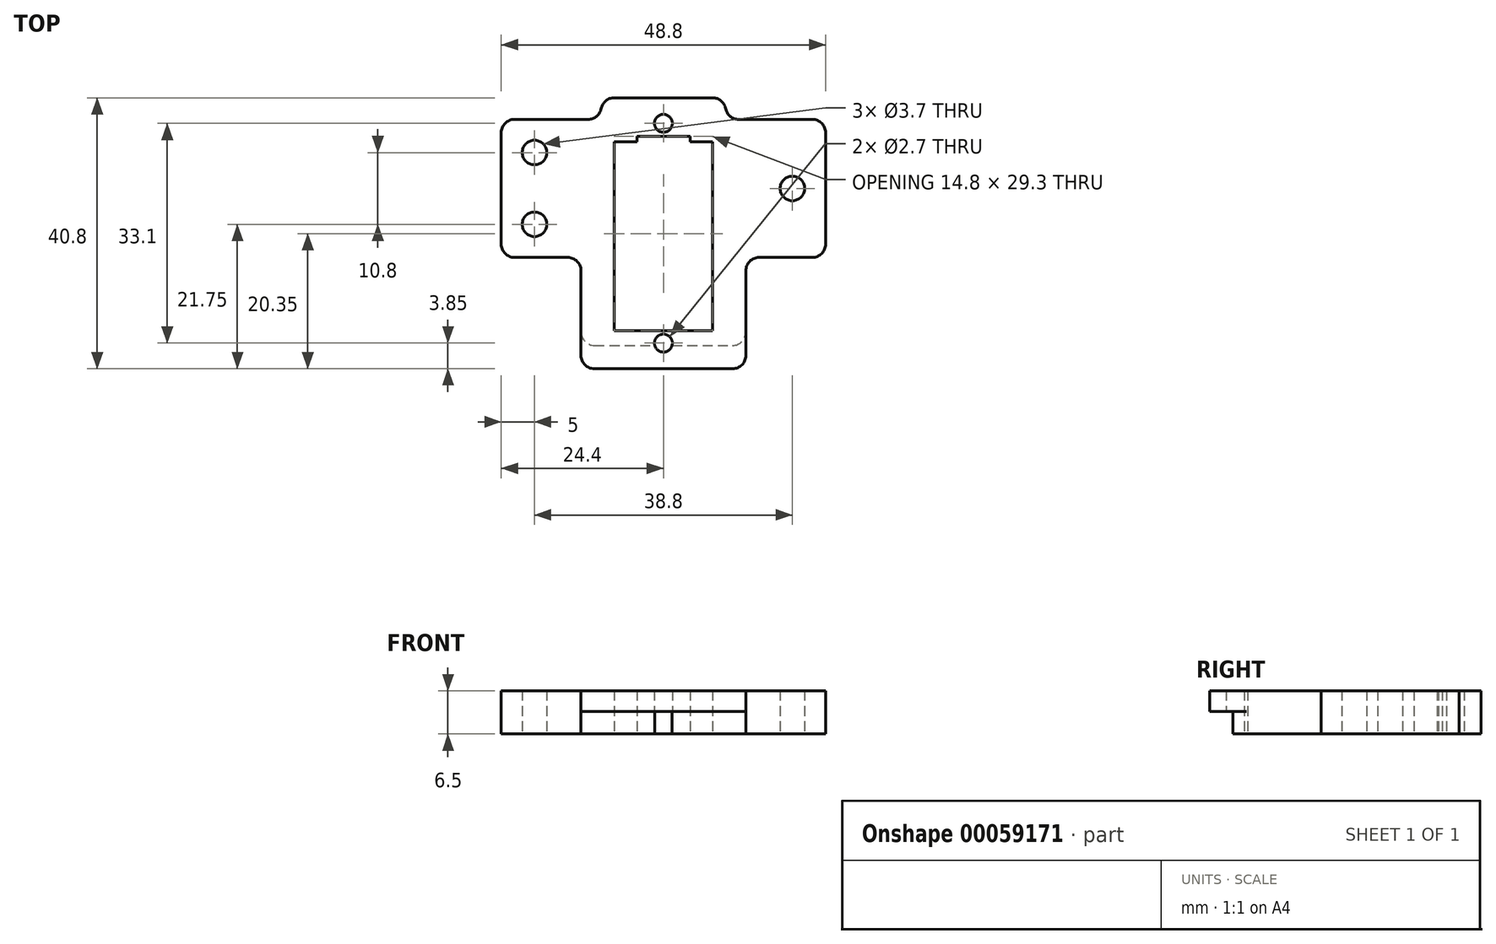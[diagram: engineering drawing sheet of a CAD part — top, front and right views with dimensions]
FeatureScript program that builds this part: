
annotation { "Feature Type Name" : "Feature", "Feature Type Description" : "" }
export const myFeature = defineFeature(function(context is Context, id is Id, definition is map)
    precondition{}
    {
        {
            var Q0;
            Q0=qCreatedBy(makeId("Top.planeOp"),FACE);
            var sketch = newSketch(context, id + "F0", { "sketchPlane" : qUnion([Q0])});
            skLineSegment(sketch, "E0.top", {"start": v(-24.4, -10.4) * mm, "end": v(24.4, -10.4) * mm});
            skLineSegment(sketch, "E0.left", {"start": v(-24.4, 10.4) * mm, "end": v(-24.4, -10.4) * mm});
            skLineSegment(sketch, "E0.right", {"start": v(24.4, 10.4) * mm, "end": v(24.4, -10.4) * mm});
            skCircle(sketch, "E1", {"center": v(-19.4, 5.4) * mm, "radius": 1.85 * mm});
            skCircle(sketch, "E2", {"center": v(-19.4, -5.4) * mm, "radius": 1.85 * mm});
            skLineSegment(sketch, "E3", {"start": v(-9.4, 10.4) * mm, "end": v(-9.4, 13.65) * mm});
            skLineSegment(sketch, "E4", {"start": v(-9.4, 13.65) * mm, "end": v(9.4, 13.65) * mm});
            skLineSegment(sketch, "E5", {"start": v(9.4, 13.65) * mm, "end": v(9.4, 10.4) * mm});
            skLineSegment(sketch, "E6", {"start": v(-9.4, 10.4) * mm, "end": v(-24.4, 10.4) * mm});
            skLineSegment(sketch, "E7", {"start": v(9.4, 10.4) * mm, "end": v(24.4, 10.4) * mm});
            skLineSegment(sketch, "E8", {"start": v(-24.4, -10.4) * mm, "end": v(-24.4, -27.15) * mm});
            skLineSegment(sketch, "E9", {"start": v(-24.4, -27.15) * mm, "end": v(24.5, -27.15) * mm});
            skLineSegment(sketch, "E10", {"start": v(24.5, -27.15) * mm, "end": v(24.4, -10.4) * mm});
            skLineSegment(sketch, "E11.bottom", {"start": v(-7.4, 7.05) * mm, "end": v(7.4, 7.05) * mm});
            skLineSegment(sketch, "E11.top", {"start": v(-7.4, -20.25) * mm, "end": v(7.4, -20.25) * mm});
            skLineSegment(sketch, "E11.left", {"start": v(-7.4, 7.05) * mm, "end": v(-7.4, -20.25) * mm});
            skLineSegment(sketch, "E11.right", {"start": v(7.4, 7.05) * mm, "end": v(7.4, -20.25) * mm});
            skCircle(sketch, "E12", {"center": v(0, 9.8) * mm, "radius": 1.35 * mm});
            skCircle(sketch, "E13", {"center": v(0, -23.3) * mm, "radius": 1.35 * mm});
            skLineSegment(sketch, "E14", {"start": v(-4, 7.05) * mm, "end": v(-4, 7.85) * mm});
            skLineSegment(sketch, "E15", {"start": v(-4, 7.85) * mm, "end": v(4, 7.85) * mm});
            skLineSegment(sketch, "E16", {"start": v(4, 7.85) * mm, "end": v(4, 7.05) * mm});
            skLineSegment(sketch, "E17", {"start": v(-24.4, -23.65) * mm, "end": v(24.48, -23.65) * mm});
            skCircle(sketch, "E18", {"center": v(-27.8, -13.35) * mm, "radius": 2.7 * mm});
            skLineSegment(sketch, "E19", {"start": v(-24.4, -10.4) * mm, "end": v(-33.3, -10.4) * mm});
            skLineSegment(sketch, "E20", {"start": v(-33.3, -10.4) * mm, "end": v(-33.3, -18.51) * mm});
            skLineSegment(sketch, "E21", {"start": v(-33.3, -18.51) * mm, "end": v(-24.4, -23.65) * mm});
            skLineSegment(sketch, "E22", {"start": v(-33.3, -10.4) * mm, "end": v(-24.4, -5.26) * mm});
            skLineSegment(sketch, "E23", {"start": v(17.4, -18.48) * mm, "end": v(17.4, -27.15) * mm});
            skLineSegment(sketch, "E24", {"start": v(17.4, -18.48) * mm, "end": v(24.4, -10.4) * mm});
            skCircle(sketch, "E25", {"center": v(19.4, 0) * mm, "radius": 1.85 * mm});
            skLineSegment(sketch, "E26", {"start": v(-7.4, -20.25) * mm, "end": v(-7.4, -21.45) * mm});
            skLineSegment(sketch, "E27", {"start": v(-7.4, -21.45) * mm, "end": v(7.4, -21.45) * mm});
            skLineSegment(sketch, "E28", {"start": v(7.4, -21.86) * mm, "end": v(7.4, -20.25) * mm});
            skLineSegment(sketch, "E29", {"start": v(-12.4, -27.15) * mm, "end": v(-12.4, -10.4) * mm});
            skLineSegment(sketch, "E30", {"start": v(12.4, -27.15) * mm, "end": v(12.4, -10.4) * mm});
            skSolve(sketch);
        }
        {
            var Q0;
            {var subQ19=sQuery(id+"F0.wireOp",EDGE,"E26");Q0=makeQuery(id+"F0.imprint","IMPRINT",FACE,{"disambiguationData":[TD([[makeQuery(id+"F0.imprint","IMPRINT",EDGE,{"derivedFrom":subQ19}),-1.0]])]});}
            var Q1;
            {var subQ10=sQuery(id+"F0.wireOp",EDGE,"E0.right");Q1=makeQuery(id+"F0.imprint","IMPRINT",FACE,{"disambiguationData":[TD([[makeQuery(id+"F0.imprint","IMPRINT",EDGE,{"derivedFrom":subQ10}),-1.0]])]});}
            extrude(context, id + "F1", {"entities" : qUnion([Q0, Q1]), "depth" : 6.5 * mm});
        }
        {
            var Q0;
            {var subQ5=sQuery(id+"F0.wireOp",EDGE,"E29");var subQ6=sQuery(id+"F0.wireOp",EDGE,"E9");var subQ7=makeQuery(id+"F0.imprint","INTERSECT",VERTEX,{"derivedFrom":[subQ6,subQ5]});Q0=makeQuery(id+"F0.imprint","IMPRINT",FACE,{"disambiguationData":[TD([[makeQuery(id+"F0.imprint","IMPRINT",EDGE,{"disambiguationData":[TD([[subQ7,-1.0]])],"derivedFrom":subQ6}),1.0]])]});}
            extrude(context, id + "F2", {"entities" : qUnion([Q0]), "operationType" : NewBodyOperationType.ADD, "depth" : 6.5 * mm, "hasSecondDirection" : true, "secondDirectionOppositeDirection" : false, "secondDirectionDepth" : 3.35 * mm});
        }
        {
            var Q0;
            Q0=makeQuery(id+"F1.opExtrude","SWEPT_EDGE",EDGE,{"disambiguationData":[OSD([sQuery(id+"F0.wireOp",EDGE,"E0.top"),sQuery(id+"F0.wireOp",EDGE,"E0.left"),sQuery(id+"F0.wireOp",EDGE,"E8"),sQuery(id+"F0.wireOp",EDGE,"E19")])]});
            var Q1;
            Q1=makeQuery(id+"F1.opExtrude","SWEPT_EDGE",EDGE,{"disambiguationData":[OSD([sQuery(id+"F0.wireOp",EDGE,"E0.left"),sQuery(id+"F0.wireOp",EDGE,"E6")])]});
            var Q2;
            Q2=makeQuery(id+"F1.opExtrude","SWEPT_EDGE",EDGE,{"disambiguationData":[OSD([sQuery(id+"F0.wireOp",EDGE,"E0.top"),sQuery(id+"F0.wireOp",EDGE,"E0.right"),sQuery(id+"F0.wireOp",EDGE,"E10"),sQuery(id+"F0.wireOp",EDGE,"E24")])]});
            var Q3;
            Q3=makeQuery(id+"F1.opExtrude","SWEPT_EDGE",EDGE,{"disambiguationData":[OSD([sQuery(id+"F0.wireOp",EDGE,"E0.right"),sQuery(id+"F0.wireOp",EDGE,"E7")])]});
            var Q4;
            Q4=makeQuery(id+"F1.opExtrude","SWEPT_EDGE",EDGE,{"disambiguationData":[OSD([sQuery(id+"F0.wireOp",EDGE,"E4"),sQuery(id+"F0.wireOp",EDGE,"E5")])]});
            var Q5;
            Q5=makeQuery(id+"F2.opExtrude","SWEPT_EDGE",EDGE,{"disambiguationData":[OSD([sQuery(id+"F0.wireOp",EDGE,"E9"),sQuery(id+"F0.wireOp",EDGE,"E29")])]});
            var Q6;
            Q6=makeQuery(id+"F1.opExtrude","SWEPT_EDGE",EDGE,{"disambiguationData":[OSD([sQuery(id+"F0.wireOp",EDGE,"E17"),sQuery(id+"F0.wireOp",EDGE,"E29")])]});
            var Q7;
            Q7=makeQuery(id+"F2.opExtrude","SWEPT_EDGE",EDGE,{"disambiguationData":[OSD([sQuery(id+"F0.wireOp",EDGE,"E9"),sQuery(id+"F0.wireOp",EDGE,"E30")])]});
            var Q8;
            Q8=makeQuery(id+"F1.opExtrude","SWEPT_EDGE",EDGE,{"disambiguationData":[OSD([sQuery(id+"F0.wireOp",EDGE,"E17"),sQuery(id+"F0.wireOp",EDGE,"E30")])]});
            var Q9;
            Q9=makeQuery(id+"F1.opExtrude","SWEPT_EDGE",EDGE,{"disambiguationData":[OSD([sQuery(id+"F0.wireOp",EDGE,"E0.top"),sQuery(id+"F0.wireOp",EDGE,"E30")])]});
            var Q10;
            Q10=makeQuery(id+"F1.opExtrude","SWEPT_EDGE",EDGE,{"disambiguationData":[OSD([sQuery(id+"F0.wireOp",EDGE,"E0.top"),sQuery(id+"F0.wireOp",EDGE,"E29")])]});
            var Q11;
            Q11=makeQuery(id+"F1.opExtrude","SWEPT_EDGE",EDGE,{"disambiguationData":[OSD([sQuery(id+"F0.wireOp",EDGE,"E3"),sQuery(id+"F0.wireOp",EDGE,"E4")])]});
            fillet(context, id + "F3", {"entities" : qUnion([Q0, Q1, Q2, Q3, Q4, Q5, Q6, Q7, Q8, Q9, Q10, Q11]), "radius" : 2 * mm, "tangentPropagation" : true, "allowEdgeOverflow" : false});
        }
        {
            var Q0;
            Q0=makeQuery(id+"F1.opExtrude","SWEPT_EDGE",EDGE,{"disambiguationData":[OSD([sQuery(id+"F0.wireOp",EDGE,"E3"),sQuery(id+"F0.wireOp",EDGE,"E6")])]});
            var Q1;
            Q1=makeQuery(id+"F1.opExtrude","SWEPT_EDGE",EDGE,{"disambiguationData":[OSD([sQuery(id+"F0.wireOp",EDGE,"E5"),sQuery(id+"F0.wireOp",EDGE,"E7")])]});
            fillet(context, id + "F4", {"entities" : qUnion([Q0, Q1]), "radius" : 2 * mm, "tangentPropagation" : true, "allowEdgeOverflow" : false});
        }
    });
